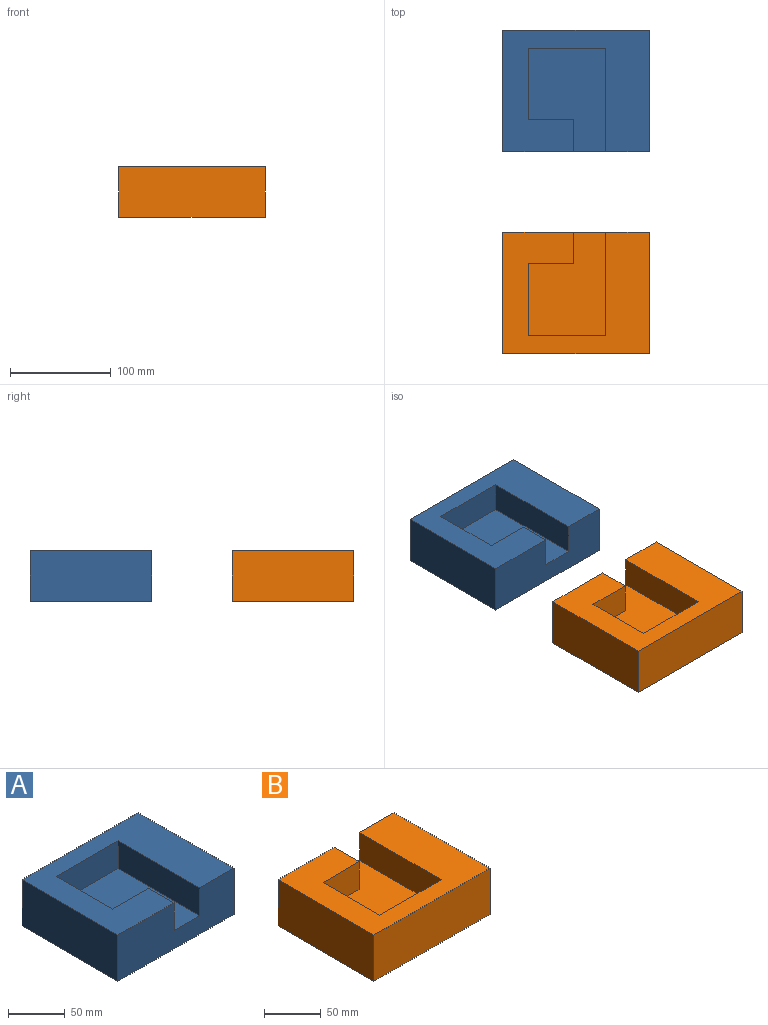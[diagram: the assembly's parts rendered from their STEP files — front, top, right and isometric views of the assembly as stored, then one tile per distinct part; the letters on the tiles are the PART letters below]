
ASSEMBLY  parts=2 mates=1
PART A: 12 faces, bbox 145x120x50 mm
  f0: plane 145x120mm, normal (0,0,1), area 10953.2mm2, adj f1,f2,f3,f4,f6,f7,f8,f9
  f1: plane 120x50mm, normal (-1,0,0), area 6000mm2, adj f0,f2,f4,f5
  f2: plane 145x50mm, normal (0,-1,0), area 6290mm2, adj f0,f1,f3,f5,f7,f8,f11
  f3: plane 120x50mm, normal (1,0,0), area 6000mm2, adj f0,f2,f4,f5
  f4: plane 145x50mm, normal (0,1,0), area 7250mm2, adj f0,f1,f3,f5
  f5: plane 145x120mm, normal (0,0,-1), area 17400mm2, adj f1,f2,f3,f4
  f6: plane 45x30mm, normal (0,1,0), area 1350mm2, adj f0,f7,f10,f11
  f7: plane 31.27x30mm, normal (1,0,0), area 938.1mm2, adj f0,f2,f6,f11
  f8: plane 102x30mm, normal (-1,0,0), area 3060mm2, adj f0,f2,f9,f11
  f9: plane 77x30mm, normal (0,-1,0), area 2310mm2, adj f0,f8,f10,f11
  f10: plane 70.73x30mm, normal (1,0,0), area 2121.9mm2, adj f0,f6,f9,f11
  f11: plane 102x77mm, normal (0,0,1), area 6446.8mm2, adj f2,f6,f7,f8,f9,f10
PART B: 12 faces, bbox 145x120x50 mm
  f0: plane 145x120mm, normal (0,0,1), area 10953.2mm2, adj f1,f2,f3,f4,f6,f7,f8,f9
  f1: plane 120x50mm, normal (-1,0,0), area 6000mm2, adj f0,f2,f4,f5
  f2: plane 145x50mm, normal (0,1,0), area 6290mm2, adj f0,f1,f3,f5,f7,f8,f11
  f3: plane 120x50mm, normal (1,0,0), area 6000mm2, adj f0,f2,f4,f5
  f4: plane 145x50mm, normal (0,-1,0), area 7250mm2, adj f0,f1,f3,f5
  f5: plane 145x120mm, normal (0,0,-1), area 17400mm2, adj f1,f2,f3,f4
  f6: plane 45x30mm, normal (0,-1,0), area 1350mm2, adj f0,f7,f10,f11
  f7: plane 31.27x30mm, normal (1,0,0), area 938.1mm2, adj f0,f2,f6,f11
  f8: plane 102x30mm, normal (-1,0,0), area 3060mm2, adj f0,f2,f9,f11
  f9: plane 77x30mm, normal (0,1,0), area 2310mm2, adj f0,f8,f10,f11
  f10: plane 70.73x30mm, normal (1,0,0), area 2121.9mm2, adj f0,f6,f9,f11
  f11: plane 102x77mm, normal (0,0,1), area 6446.8mm2, adj f2,f6,f7,f8,f9,f10
PLACE A t=(0,200,0)mm
PLACE B t=(0,170,0)mm
MATE parallel A.f1 <-> B.f1  axis (-1,0,0) through (0,260,25)mm
